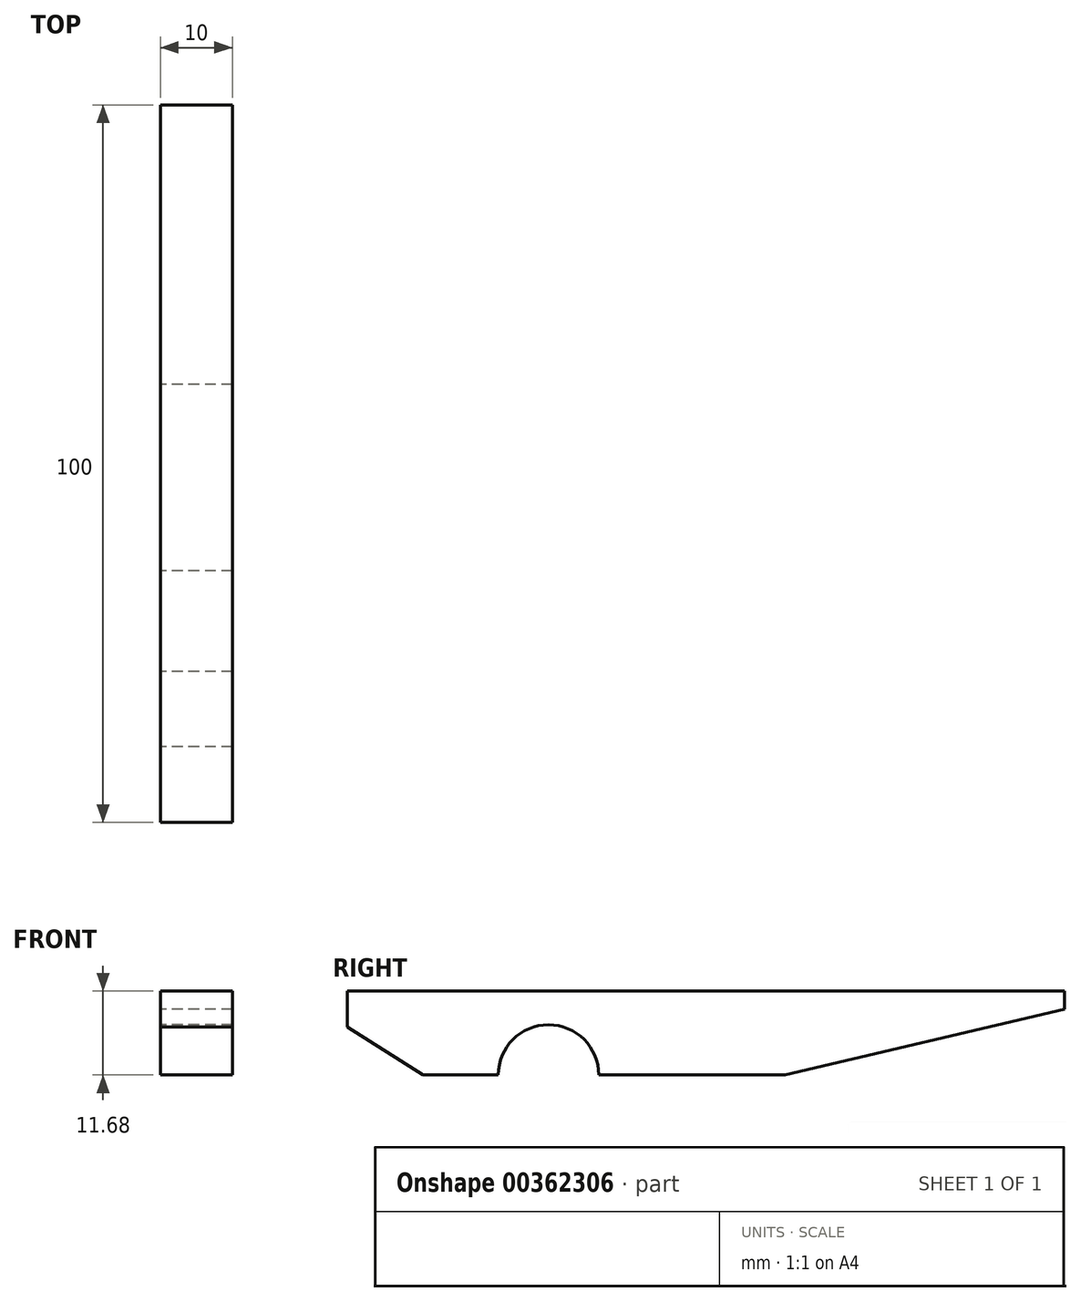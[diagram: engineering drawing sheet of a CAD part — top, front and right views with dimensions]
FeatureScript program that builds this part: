
annotation { "Feature Type Name" : "Feature", "Feature Type Description" : "" }
export const myFeature = defineFeature(function(context is Context, id is Id, definition is map)
    precondition{}
    {
        {
            var Q0;
            Q0=qCreatedBy(makeId("Right.planeOp"),FACE);
            var sketch = newSketch(context, id + "F0", { "sketchPlane" : qUnion([Q0])});
            skLineSegment(sketch, "E0", {"start": v(-48.28, 11.68) * mm, "end": v(51.72, 11.68) * mm});
            skLineSegment(sketch, "E1", {"start": v(51.72, 11.68) * mm, "end": v(51.72, 9.18) * mm});
            skLineSegment(sketch, "E2", {"start": v(51.72, 9.18) * mm, "end": v(12.79, 0) * mm});
            skLineSegment(sketch, "E3", {"start": v(12.79, 0) * mm, "end": v(-20.21, 0) * mm});
            skCircle(sketch, "E4", {"center": v(-20.21, 0) * mm, "radius": 7 * mm});
            skLineSegment(sketch, "E5", {"start": v(-20.21, 0) * mm, "end": v(-37.71, 0) * mm});
            skLineSegment(sketch, "E6", {"start": v(-48.28, 11.68) * mm, "end": v(-48.28, 6.68) * mm});
            skLineSegment(sketch, "E7", {"start": v(-37.71, 0) * mm, "end": v(-48.28, 6.68) * mm});
            skSolve(sketch);
        }
        {
            var Q0;
            Q0=makeQuery(id+"F0.imprint","IMPRINT",FACE,{"disambiguationData":[TD([[makeQuery(id+"F0.imprint","IMPRINT",EDGE,{"derivedFrom":sQuery(id+"F0.wireOp",EDGE,"E0")}),-1.0]])]});
            extrude(context, id + "F1", {"entities" : qUnion([Q0]), "endBound" : BoundingType.SYMMETRIC, "depth" : 10 * mm});
        }
    });
